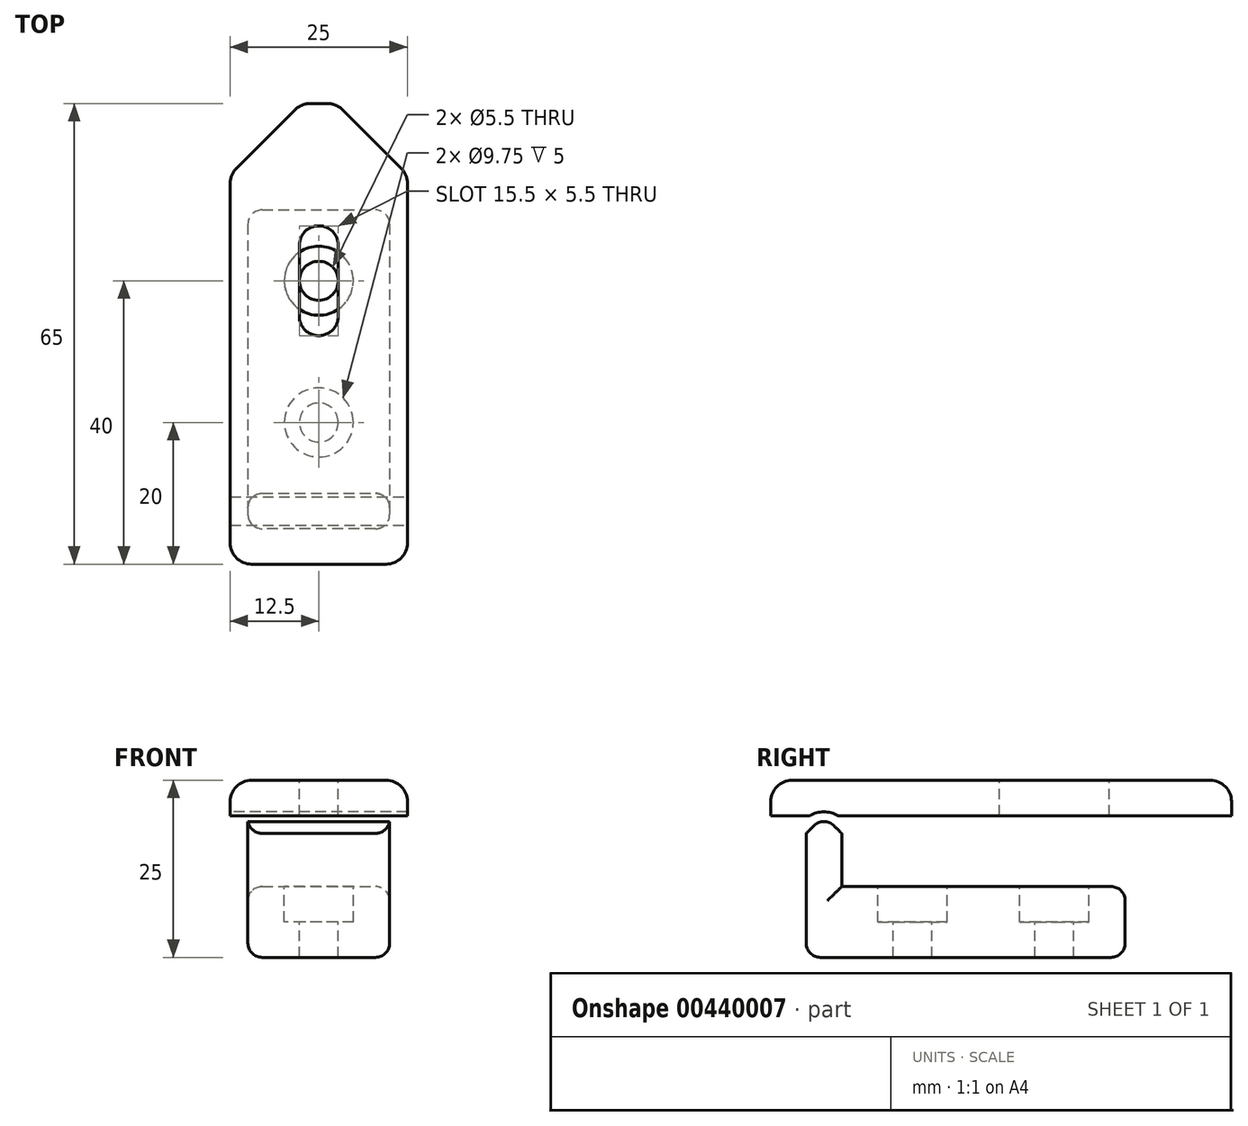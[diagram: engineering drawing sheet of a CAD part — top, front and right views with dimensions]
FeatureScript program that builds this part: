
annotation { "Feature Type Name" : "Feature", "Feature Type Description" : "" }
export const myFeature = defineFeature(function(context is Context, id is Id, definition is map)
    precondition{}
    {
        {
            var Q0;
            Q0=qCreatedBy(makeId("Top.planeOp"),FACE);
            var sketch = newSketch(context, id + "F0", { "sketchPlane" : qUnion([Q0])});
            skLineSegment(sketch, "E0.bottom", {"start": v(-10, 20) * mm, "end": v(10, 20) * mm});
            skLineSegment(sketch, "E0.top", {"start": v(-10, -20) * mm, "end": v(10, -20) * mm});
            skLineSegment(sketch, "E0.left", {"start": v(-10, 20) * mm, "end": v(-10, -20) * mm});
            skLineSegment(sketch, "E0.right", {"start": v(10, 20) * mm, "end": v(10, -20) * mm});
            skPoint(sketch, "E0.middle", {"position": v(0, 0) * mm});
            skCircle(sketch, "E1", {"center": v(0, 10) * mm, "radius": 5 * mm, "construction": true});
            skCircle(sketch, "E2", {"center": v(0, -10) * mm, "radius": 5 * mm, "construction": true});
            skLineSegment(sketch, "E3", {"start": v(0, 10) * mm, "end": v(0, 0) * mm, "construction": true});
            skLineSegment(sketch, "E4", {"start": v(0, 0) * mm, "end": v(0, -10) * mm, "construction": true});
            skLineSegment(sketch, "E5", {"start": v(0, 10) * mm, "end": v(-10, 10) * mm, "construction": true});
            skLineSegment(sketch, "E6", {"start": v(0, 10) * mm, "end": v(10, 10) * mm, "construction": true});
            skLineSegment(sketch, "E7.top", {"start": v(-10, -25) * mm, "end": v(10, -25) * mm});
            skLineSegment(sketch, "E7.left", {"start": v(-10, -20) * mm, "end": v(-10, -25) * mm});
            skLineSegment(sketch, "E7.right", {"start": v(10, -20) * mm, "end": v(10, -25) * mm});
            skSolve(sketch);
        }
        {
            var Q0;
            Q0=makeQuery(id+"F0.imprint","IMPRINT",FACE,{"disambiguationData":[TD([[makeQuery(id+"F0.imprint","IMPRINT",EDGE,{"derivedFrom":sQuery(id+"F0.wireOp",EDGE,"E0.bottom")}),-1.0]])]});
            extrude(context, id + "F1", {"entities" : qUnion([Q0]), "depth" : 10 * mm});
        }
        {
            var Q0;
            Q0=makeQuery(id+"F0.imprint","IMPRINT",FACE,{"disambiguationData":[TD([[makeQuery(id+"F0.imprint","IMPRINT",EDGE,{"derivedFrom":sQuery(id+"F0.wireOp",EDGE,"E0.top")}),-1.0]])]});
            extrude(context, id + "F2", {"entities" : qUnion([Q0]), "operationType" : NewBodyOperationType.ADD, "depth" : 20 * mm});
        }
        {
            var Q0;
            Q0=makeQuery(id+"F1.opExtrude","CAP_FACE",FACE,{"disambiguationData":[OSD([sQuery(id+"F0.wireOp",EDGE,"E0.bottom"),sQuery(id+"F0.wireOp",EDGE,"E0.left"),sQuery(id+"F0.wireOp",EDGE,"E0.right"),sQuery(id+"F0.wireOp",EDGE,"E0.top")])],"isStart":false});
            var sketch = newSketch(context, id + "F3", { "sketchPlane" : qUnion([Q0])});
            skPoint(sketch, "E8", {"position": v(0, 10) * mm});
            skPoint(sketch, "E9", {"position": v(0, -10) * mm});
            skSolve(sketch);
        }
        {
            var Q0;
            Q0=makeQuery(id+"F2.opExtrude","CAP_EDGE",EDGE,{"disambiguationData":[OSD([sQuery(id+"F0.wireOp",EDGE,"E7.top")])],"isStart":false});
            var Q1;
            Q1=makeQuery(id+"F2.opExtrude","CAP_EDGE",EDGE,{"disambiguationData":[OSD([sQuery(id+"F0.wireOp",EDGE,"E0.top")])],"isStart":false});
            chamfer(context, id + "F4", {"entities" : qUnion([Q0, Q1]), "width" : 2.5 * mm, "tangentPropagation" : true});
        }
        {
            var Q0;
            Q0=makeQuery(id+"F4.opChamfer","BLEND_EDGE",EDGE,{"blendedFrom":[makeQuery(id+"F2.opExtrude","CAP_EDGE",EDGE,{"disambiguationData":[OSD([sQuery(id+"F0.wireOp",EDGE,"E0.top")])],"isStart":false}),makeQuery(id+"F2.opExtrude","CAP_EDGE",EDGE,{"disambiguationData":[OSD([sQuery(id+"F0.wireOp",EDGE,"E7.top")])],"isStart":false})],"blendedInto":[]});
            fillet(context, id + "F5", {"entities" : qUnion([Q0]), "radius" : 2 * mm, "tangentPropagation" : true, "allowEdgeOverflow" : false});
        }
        {
            var Q0;
            Q0=sQuery(id+"F3.wireOp",VERTEX,"E9");
            var Q1;
            Q1=sQuery(id+"F3.wireOp",VERTEX,"E8");
            var Q2;
            Q2=makeQuery(id+"F1.opExtrude","SWEPT_BODY",BODY,{"disambiguationData":[OSD([sQuery(id+"F0.wireOp",EDGE,"E0.bottom"),sQuery(id+"F0.wireOp",EDGE,"E0.left"),sQuery(id+"F0.wireOp",EDGE,"E0.right"),sQuery(id+"F0.wireOp",EDGE,"E0.top")])]});
            hole(context, id + "F6", {"style" : HoleStyle.C_BORE, "endStyle" : HoleEndStyle.THROUGH, "standardTappedOrClearance" : lookupTablePath({ "standard" : "ISO", "fit" : "Normal", "size" : "M5", "type" : "Clearance" }), "standardBlindInLast" : lookupTablePath({ "fit" : "Standard", "standard" : "ISO", "size" : "M5", "type" : "Clearance" }), "holeDiameter" : 5.5 * mm, "cBoreDiameter" : 9.75 * mm, "cBoreDepth" : 5 * mm, "isTappedThrough" : true, "tappedDepth" : 13.2 * mm, "tapClearance" : 3, "startFromSketch" : true, "locations" : qUnion([Q0, Q1]), "scope" : qUnion([Q2])});
        }
        {
            var Q0;
            Q0=makeQuery(id+"F2.opExtrude","SWEPT_EDGE",EDGE,{"disambiguationData":[OSD([sQuery(id+"F0.wireOp",EDGE,"E7.top"),sQuery(id+"F0.wireOp",EDGE,"E7.right")])]});
            var Q1;
            Q1=makeQuery(id+"F2.opExtrude","SWEPT_EDGE",EDGE,{"disambiguationData":[OSD([sQuery(id+"F0.wireOp",EDGE,"E0.right"),sQuery(id+"F0.wireOp",EDGE,"E0.top"),sQuery(id+"F0.wireOp",EDGE,"E7.right")])]});
            var Q2;
            Q2=makeQuery(id+"F1.opExtrude","CAP_EDGE",EDGE,{"disambiguationData":[OSD([sQuery(id+"F0.wireOp",EDGE,"E0.right")])],"isStart":false});
            var Q3;
            Q3=makeQuery(id+"F2.opExtrude","SWEPT_EDGE",EDGE,{"disambiguationData":[OSD([sQuery(id+"F0.wireOp",EDGE,"E0.left"),sQuery(id+"F0.wireOp",EDGE,"E0.top"),sQuery(id+"F0.wireOp",EDGE,"E7.left")])]});
            var Q4;
            Q4=makeQuery(id+"F2.opExtrude","SWEPT_EDGE",EDGE,{"disambiguationData":[OSD([sQuery(id+"F0.wireOp",EDGE,"E7.top"),sQuery(id+"F0.wireOp",EDGE,"E7.left")])]});
            var Q5;
            Q5=makeQuery(id+"F1.opExtrude","CAP_EDGE",EDGE,{"disambiguationData":[OSD([sQuery(id+"F0.wireOp",EDGE,"E0.left")])],"isStart":false});
            var Q6;
            Q6=makeQuery(id+"F1.opExtrude","CAP_EDGE",EDGE,{"disambiguationData":[OSD([sQuery(id+"F0.wireOp",EDGE,"E0.bottom")])],"isStart":false});
            var Q7;
            Q7=makeQuery(id+"F1.opExtrude","SWEPT_EDGE",EDGE,{"disambiguationData":[OSD([sQuery(id+"F0.wireOp",EDGE,"E0.bottom"),sQuery(id+"F0.wireOp",EDGE,"E0.right")])]});
            var Q8;
            Q8=makeQuery(id+"F1.opExtrude","SWEPT_EDGE",EDGE,{"disambiguationData":[OSD([sQuery(id+"F0.wireOp",EDGE,"E0.bottom"),sQuery(id+"F0.wireOp",EDGE,"E0.left")])]});
            var Q9;
            Q9=makeQuery(id+"F1.opExtrude","CAP_EDGE",EDGE,{"disambiguationData":[OSD([sQuery(id+"F0.wireOp",EDGE,"E0.bottom")])],"isStart":true});
            var Q10;
            Q10=makeQuery(id+"F2.boolean.opBoolean","MERGE",EDGE,{"derivedFrom":[makeQuery(id+"F1.opExtrude","CAP_EDGE",EDGE,{"disambiguationData":[OSD([sQuery(id+"F0.wireOp",EDGE,"E0.right")])],"isStart":true}),makeQuery(id+"F2.opExtrude","CAP_EDGE",EDGE,{"disambiguationData":[OSD([sQuery(id+"F0.wireOp",EDGE,"E7.right")])],"isStart":true})]});
            var Q11;
            Q11=makeQuery(id+"F2.opExtrude","CAP_EDGE",EDGE,{"disambiguationData":[OSD([sQuery(id+"F0.wireOp",EDGE,"E7.top")])],"isStart":true});
            var Q12;
            Q12=makeQuery(id+"F2.boolean.opBoolean","MERGE",EDGE,{"derivedFrom":[makeQuery(id+"F1.opExtrude","CAP_EDGE",EDGE,{"disambiguationData":[OSD([sQuery(id+"F0.wireOp",EDGE,"E0.left")])],"isStart":true}),makeQuery(id+"F2.opExtrude","CAP_EDGE",EDGE,{"disambiguationData":[OSD([sQuery(id+"F0.wireOp",EDGE,"E7.left")])],"isStart":true})]});
            fillet(context, id + "F7", {"entities" : qUnion([Q0, Q1, Q2, Q3, Q4, Q5, Q6, Q7, Q8, Q9, Q10, Q11, Q12]), "radius" : 2 * mm, "tangentPropagation" : true, "allowEdgeOverflow" : false});
        }
        {
            var Q0;
            Q0=makeQuery(id+"F1.opExtrude","CAP_FACE",FACE,{"disambiguationData":[OSD([sQuery(id+"F0.wireOp",EDGE,"E0.bottom"),sQuery(id+"F0.wireOp",EDGE,"E0.left"),sQuery(id+"F0.wireOp",EDGE,"E0.right"),sQuery(id+"F0.wireOp",EDGE,"E0.top")])],"isStart":false});
            cPlane(context, id + "F8", {"entities" : qUnion([Q0]), "cplaneType" : CPlaneType.OFFSET, "offset" : 10 * mm, "width" : 150 * mm, "height" : 150 * mm});
        }
        {
            var Q0;
            Q0=qCreatedBy(id+"F8.planeOp",FACE);
            var sketch = newSketch(context, id + "F9", { "sketchPlane" : qUnion([Q0])});
            skLineSegment(sketch, "E10.bottom", {"start": v(-12.5, 35) * mm, "end": v(12.5, 35) * mm});
            skLineSegment(sketch, "E10.top", {"start": v(-12.5, -30) * mm, "end": v(12.5, -30) * mm});
            skLineSegment(sketch, "E10.left", {"start": v(-12.5, 35) * mm, "end": v(-12.5, -30) * mm});
            skLineSegment(sketch, "E10.right", {"start": v(12.5, 35) * mm, "end": v(12.5, -30) * mm});
            skSolve(sketch);
        }
        {
            var Q0;
            Q0=makeQuery(id+"F9.imprint","IMPRINT",FACE,{"disambiguationData":[TD([[makeQuery(id+"F9.imprint","IMPRINT",EDGE,{"derivedFrom":sQuery(id+"F9.wireOp",EDGE,"E10.bottom")}),-1.0]])]});
            extrude(context, id + "F10", {"entities" : qUnion([Q0]), "depth" : 5 * mm});
        }
        {
            var Q0;
            Q0=makeQuery(id+"F10.opExtrude","SWEPT_FACE",FACE,{"disambiguationData":[OSD([sQuery(id+"F9.wireOp",EDGE,"E10.right")])]});
            var sketch = newSketch(context, id + "F11", { "sketchPlane" : qUnion([Q0])});
            skPoint(sketch, "E11", {"position": v(-22.5, 20) * mm});
            skPoint(sketch, "E12", {"position": v(-22.5, 19.17) * mm});
            skLineSegment(sketch, "E13", {"start": v(-22.5, 22) * mm, "end": v(-24.5, 20) * mm});
            skLineSegment(sketch, "E14", {"start": v(-22.5, 22) * mm, "end": v(-20.5, 20) * mm});
            skSolve(sketch);
        }
        {
            var Q0;
            {var subQ0=sQuery(id+"F11.wireOp",EDGE,"E13");Q0=makeQuery(id+"F11.imprint","IMPRINT",FACE,{"disambiguationData":[TD([[makeQuery(id+"F11.imprint","IMPRINT",EDGE,{"derivedFrom":subQ0}),1.0]])]});}
            extrude(context, id + "F12", {"entities" : qUnion([Q0]), "operationType" : NewBodyOperationType.REMOVE, "endBound" : BoundingType.UP_TO_NEXT, "oppositeDirection" : true, "depth" : 25 * mm});
        }
        {
            var Q0;
            Q0=makeQuery(id+"F12.boolean.opBoolean","COPY",EDGE,{"derivedFrom":makeQuery(id+"F12.opExtrude","SWEPT_EDGE",EDGE,{"disambiguationData":[OSD([sQuery(id+"F11.wireOp",EDGE,"E13"),sQuery(id+"F11.wireOp",EDGE,"E14")])]})});
            fillet(context, id + "F13", {"entities" : qUnion([Q0]), "radius" : 4 * mm, "tangentPropagation" : true, "allowEdgeOverflow" : false});
        }
        {
            var Q0;
            Q0=makeQuery(id+"F10.opExtrude","CAP_FACE",FACE,{"disambiguationData":[OSD([sQuery(id+"F9.wireOp",EDGE,"E10.bottom"),sQuery(id+"F9.wireOp",EDGE,"E10.top"),sQuery(id+"F9.wireOp",EDGE,"E10.left"),sQuery(id+"F9.wireOp",EDGE,"E10.right")])],"isStart":false});
            var sketch = newSketch(context, id + "F14", { "sketchPlane" : qUnion([Q0])});
            skArc(sketch, "E15", {"start": v(-2.75, 5) * mm, "mid": v(0, 2.25) * mm, "end": v(2.75, 5) * mm});
            skArc(sketch, "E16", {"start": v(2.75, 15) * mm, "mid": v(0, 17.75) * mm, "end": v(-2.75, 15) * mm});
            skLineSegment(sketch, "E17", {"start": v(-2.75, 5) * mm, "end": v(-2.75, 15) * mm});
            skLineSegment(sketch, "E18", {"start": v(2.75, 5) * mm, "end": v(2.75, 15) * mm});
            skPoint(sketch, "E19", {"position": v(0, 10) * mm});
            skLineSegment(sketch, "E20", {"start": v(0, 10) * mm, "end": v(0, 15) * mm, "construction": true});
            skLineSegment(sketch, "E21", {"start": v(0, 10) * mm, "end": v(0, 5) * mm, "construction": true});
            skSolve(sketch);
        }
        {
            var Q0;
            Q0=makeQuery(id+"F10.opExtrude","SWEPT_EDGE",EDGE,{"disambiguationData":[OSD([sQuery(id+"F9.wireOp",EDGE,"E10.bottom"),sQuery(id+"F9.wireOp",EDGE,"E10.right")])]});
            var Q1;
            Q1=makeQuery(id+"F10.opExtrude","SWEPT_EDGE",EDGE,{"disambiguationData":[OSD([sQuery(id+"F9.wireOp",EDGE,"E10.bottom"),sQuery(id+"F9.wireOp",EDGE,"E10.left")])]});
            chamfer(context, id + "F15", {"entities" : qUnion([Q0, Q1]), "width" : 10 * mm, "tangentPropagation" : true});
        }
        {
            var Q0;
            Q0=makeQuery(id+"F10.opExtrude","SWEPT_EDGE",EDGE,{"disambiguationData":[OSD([sQuery(id+"F9.wireOp",EDGE,"E10.top"),sQuery(id+"F9.wireOp",EDGE,"E10.right")])]});
            var Q1;
            Q1=makeQuery(id+"F10.opExtrude","SWEPT_EDGE",EDGE,{"disambiguationData":[OSD([sQuery(id+"F9.wireOp",EDGE,"E10.top"),sQuery(id+"F9.wireOp",EDGE,"E10.left")])]});
            var Q2;
            Q2=makeQuery(id+"F10.opExtrude","SWEPT_EDGE",EDGE,{"disambiguationData":[OSD([sQuery(id+"F9.wireOp",EDGE,"E10.bottom"),sQuery(id+"F9.wireOp",EDGE,"E10.left")])]});
            var Q3;
            Q3=makeQuery(id+"F10.opExtrude","SWEPT_EDGE",EDGE,{"disambiguationData":[OSD([sQuery(id+"F9.wireOp",EDGE,"E10.bottom"),sQuery(id+"F9.wireOp",EDGE,"E10.right")])]});
            var Q4;
            Q4=makeQuery(id+"F10.opExtrude","CAP_EDGE",EDGE,{"disambiguationData":[OSD([sQuery(id+"F9.wireOp",EDGE,"E10.right")])],"isStart":false});
            var Q5;
            Q5=makeQuery(id+"F10.opExtrude","CAP_EDGE",EDGE,{"disambiguationData":[OSD([sQuery(id+"F9.wireOp",EDGE,"E10.bottom")])],"isStart":false});
            var Q6;
            Q6=makeQuery(id+"F10.opExtrude","CAP_EDGE",EDGE,{"disambiguationData":[OSD([sQuery(id+"F9.wireOp",EDGE,"E10.left")])],"isStart":false});
            var Q7;
            Q7=makeQuery(id+"F10.opExtrude","CAP_EDGE",EDGE,{"disambiguationData":[OSD([sQuery(id+"F9.wireOp",EDGE,"E10.top")])],"isStart":false});
            var Q8;
            {var subQ0=sQuery(id+"F9.wireOp",EDGE,"E10.right");Q8=makeQuery(id+"F15.opChamfer","BLEND_EDGE",EDGE,{"blendedFrom":[makeQuery(id+"F10.opExtrude","SWEPT_EDGE",EDGE,{"disambiguationData":[OSD([sQuery(id+"F9.wireOp",EDGE,"E10.bottom"),subQ0])]}),makeQuery(id+"F10.opExtrude","SWEPT_FACE",FACE,{"disambiguationData":[OSD([subQ0])]})],"blendedInto":[makeQuery(id+"F10.opExtrude","SWEPT_FACE",FACE,{"disambiguationData":[OSD([subQ0])]})]});}
            var Q9;
            {var subQ0=sQuery(id+"F9.wireOp",EDGE,"E10.bottom");Q9=makeQuery(id+"F15.opChamfer","BLEND_EDGE",EDGE,{"blendedFrom":[makeQuery(id+"F10.opExtrude","SWEPT_EDGE",EDGE,{"disambiguationData":[OSD([subQ0,sQuery(id+"F9.wireOp",EDGE,"E10.right")])]}),makeQuery(id+"F10.opExtrude","SWEPT_FACE",FACE,{"disambiguationData":[OSD([subQ0])]})],"blendedInto":[makeQuery(id+"F10.opExtrude","SWEPT_FACE",FACE,{"disambiguationData":[OSD([subQ0])]})]});}
            var Q10;
            {var subQ0=sQuery(id+"F9.wireOp",EDGE,"E10.right");var subQ1=sQuery(id+"F9.wireOp",EDGE,"E10.bottom");Q10=makeQuery(id+"F15.opChamfer","BLEND_EDGE",EDGE,{"blendedFrom":[makeQuery(id+"F10.opExtrude","SWEPT_EDGE",EDGE,{"disambiguationData":[OSD([subQ1,subQ0])]}),makeQuery(id+"F10.opExtrude","CAP_FACE",FACE,{"disambiguationData":[OSD([subQ1,sQuery(id+"F9.wireOp",EDGE,"E10.top"),sQuery(id+"F9.wireOp",EDGE,"E10.left"),subQ0])],"isStart":false})],"blendedInto":[makeQuery(id+"F10.opExtrude","CAP_FACE",FACE,{"disambiguationData":[OSD([subQ1,sQuery(id+"F9.wireOp",EDGE,"E10.top"),sQuery(id+"F9.wireOp",EDGE,"E10.left"),subQ0])],"isStart":false})]});}
            var Q11;
            {var subQ0=sQuery(id+"F9.wireOp",EDGE,"E10.left");Q11=makeQuery(id+"F15.opChamfer","BLEND_EDGE",EDGE,{"blendedFrom":[makeQuery(id+"F10.opExtrude","SWEPT_EDGE",EDGE,{"disambiguationData":[OSD([sQuery(id+"F9.wireOp",EDGE,"E10.bottom"),subQ0])]}),makeQuery(id+"F10.opExtrude","SWEPT_FACE",FACE,{"disambiguationData":[OSD([subQ0])]})],"blendedInto":[makeQuery(id+"F10.opExtrude","SWEPT_FACE",FACE,{"disambiguationData":[OSD([subQ0])]})]});}
            var Q12;
            {var subQ0=sQuery(id+"F9.wireOp",EDGE,"E10.bottom");Q12=makeQuery(id+"F15.opChamfer","BLEND_EDGE",EDGE,{"blendedFrom":[makeQuery(id+"F10.opExtrude","SWEPT_EDGE",EDGE,{"disambiguationData":[OSD([subQ0,sQuery(id+"F9.wireOp",EDGE,"E10.left")])]}),makeQuery(id+"F10.opExtrude","SWEPT_FACE",FACE,{"disambiguationData":[OSD([subQ0])]})],"blendedInto":[makeQuery(id+"F10.opExtrude","SWEPT_FACE",FACE,{"disambiguationData":[OSD([subQ0])]})]});}
            var Q13;
            {var subQ0=sQuery(id+"F9.wireOp",EDGE,"E10.left");var subQ1=sQuery(id+"F9.wireOp",EDGE,"E10.bottom");Q13=makeQuery(id+"F15.opChamfer","BLEND_EDGE",EDGE,{"blendedFrom":[makeQuery(id+"F10.opExtrude","SWEPT_EDGE",EDGE,{"disambiguationData":[OSD([subQ1,subQ0])]}),makeQuery(id+"F10.opExtrude","CAP_FACE",FACE,{"disambiguationData":[OSD([subQ1,sQuery(id+"F9.wireOp",EDGE,"E10.top"),subQ0,sQuery(id+"F9.wireOp",EDGE,"E10.right")])],"isStart":false})],"blendedInto":[makeQuery(id+"F10.opExtrude","CAP_FACE",FACE,{"disambiguationData":[OSD([subQ1,sQuery(id+"F9.wireOp",EDGE,"E10.top"),subQ0,sQuery(id+"F9.wireOp",EDGE,"E10.right")])],"isStart":false})]});}
            fillet(context, id + "F16", {"entities" : qUnion([Q0, Q1, Q2, Q3, Q4, Q5, Q6, Q7, Q8, Q9, Q10, Q11, Q12, Q13]), "radius" : 3 * mm, "tangentPropagation" : true, "allowEdgeOverflow" : false});
        }
        {
            var Q0;
            Q0=makeQuery(id+"F14.imprint","IMPRINT",FACE,{"disambiguationData":[TD([[makeQuery(id+"F14.imprint","IMPRINT",EDGE,{"derivedFrom":sQuery(id+"F14.wireOp",EDGE,"E15")}),1.0]])]});
            extrude(context, id + "F17", {"entities" : qUnion([Q0]), "operationType" : NewBodyOperationType.REMOVE, "endBound" : BoundingType.UP_TO_NEXT, "oppositeDirection" : true, "depth" : 25 * mm});
        }
    });
